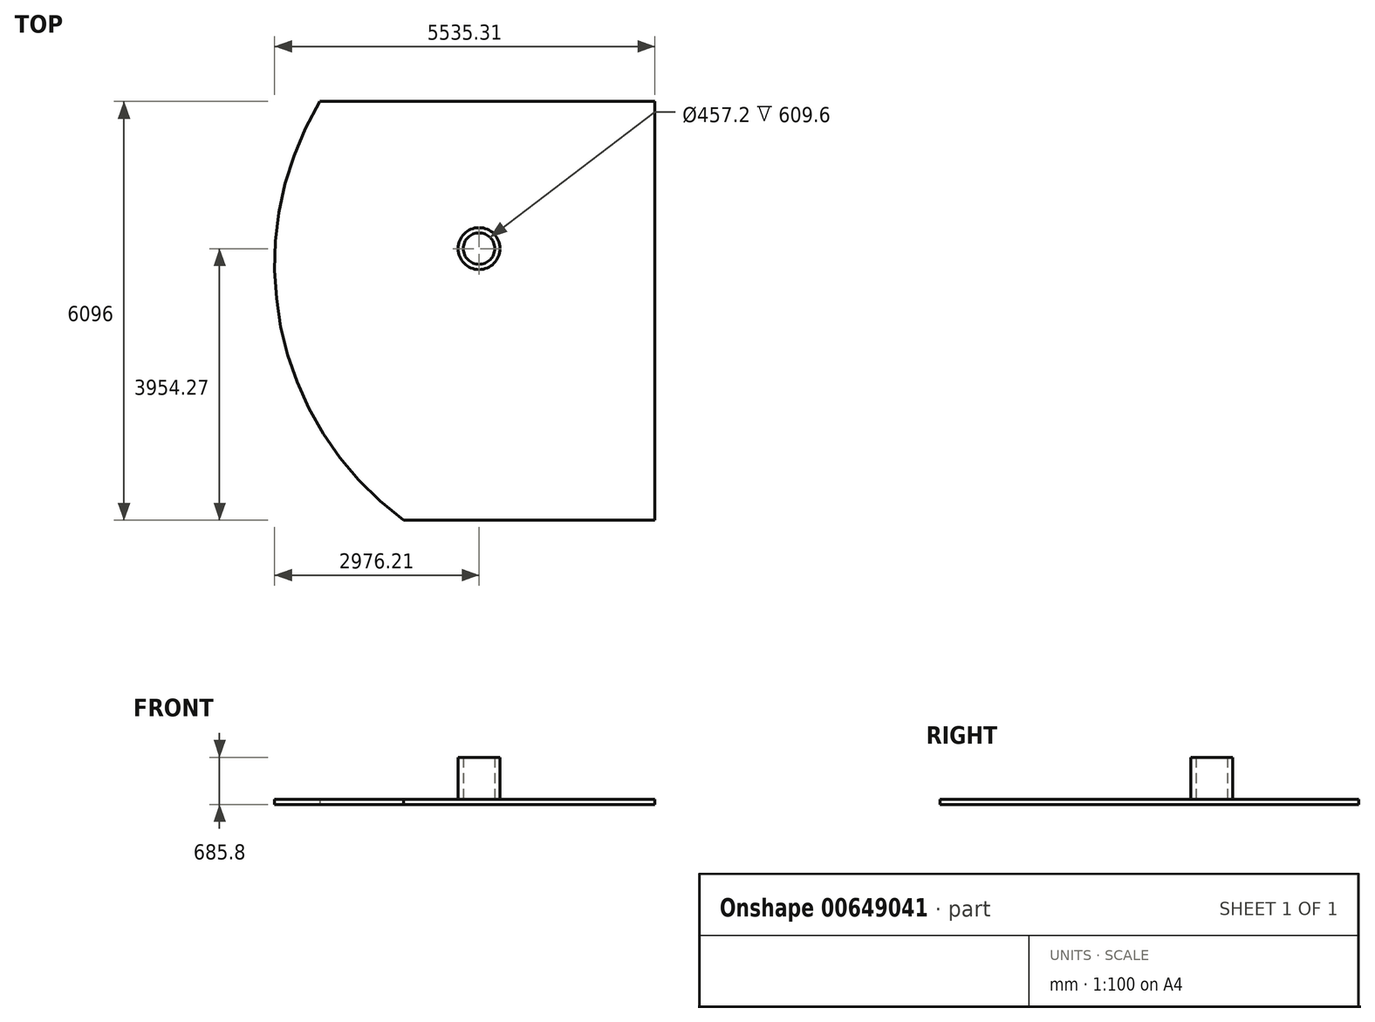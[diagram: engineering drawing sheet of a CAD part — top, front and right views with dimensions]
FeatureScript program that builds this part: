
annotation { "Feature Type Name" : "Feature", "Feature Type Description" : "" }
export const myFeature = defineFeature(function(context is Context, id is Id, definition is map)
    precondition{}
    {
        {
            var Q0;
            Q0=qCreatedBy(makeId("Top.planeOp"),FACE);
            var sketch = newSketch(context, id + "F0", { "sketchPlane" : qUnion([Q0])});
            skLineSegment(sketch, "E0", {"start": v(3048, 3048) * mm, "end": v(3048, -3048) * mm});
            skLineSegment(sketch, "E1", {"start": v(3048, 3048) * mm, "end": v(-1828.8, 3048) * mm});
            skLineSegment(sketch, "E2", {"start": v(3048, -3048) * mm, "end": v(-609.6, -3048) * mm});
            skLineSegment(sketch, "E3", {"start": v(3048, 0) * mm, "end": v(-2438.4, 0) * mm, "construction": true});
            skArc(sketch, "E4", {"start": v(-1828.8, 3048) * mm, "mid": v(-2397.58, -235.68) * mm, "end": v(-609.6, -3048) * mm});
            skSolve(sketch);
        }
        {
            var Q0;
            Q0=makeQuery(id+"F0.imprint","IMPRINT",FACE,{"disambiguationData":[TD([[makeQuery(id+"F0.imprint","IMPRINT",EDGE,{"derivedFrom":sQuery(id+"F0.wireOp",EDGE,"E0")}),-1.0]])]});
            extrude(context, id + "F1", {"entities" : qUnion([Q0]), "depth" : 76.2 * mm, "offsetDistance" : 30.48 * mm});
        }
        {
            var Q0;
            Q0=makeQuery(id+"F1.opExtrude","CAP_FACE",FACE,{"disambiguationData":[OSD([sQuery(id+"F0.wireOp",EDGE,"E0"),sQuery(id+"F0.wireOp",EDGE,"E1"),sQuery(id+"F0.wireOp",EDGE,"E2"),sQuery(id+"F0.wireOp",EDGE,"E4")])],"isStart":false});
            var sketch = newSketch(context, id + "F2", { "sketchPlane" : qUnion([Q0])});
            skCircle(sketch, "E5", {"center": v(488.9, 906.27) * mm, "radius": 304.8 * mm});
            skCircle(sketch, "E6", {"center": v(488.9, 906.27) * mm, "radius": 228.6 * mm});
            skSolve(sketch);
        }
        {
            var Q0;
            Q0 = qSketchRegion(id + "F2", true);
            extrude(context, id + "F3", {"entities" : qUnion([Q0]), "operationType" : NewBodyOperationType.ADD, "depth" : 609.6 * mm, "offsetDistance" : 30.48 * mm});
        }
    });
